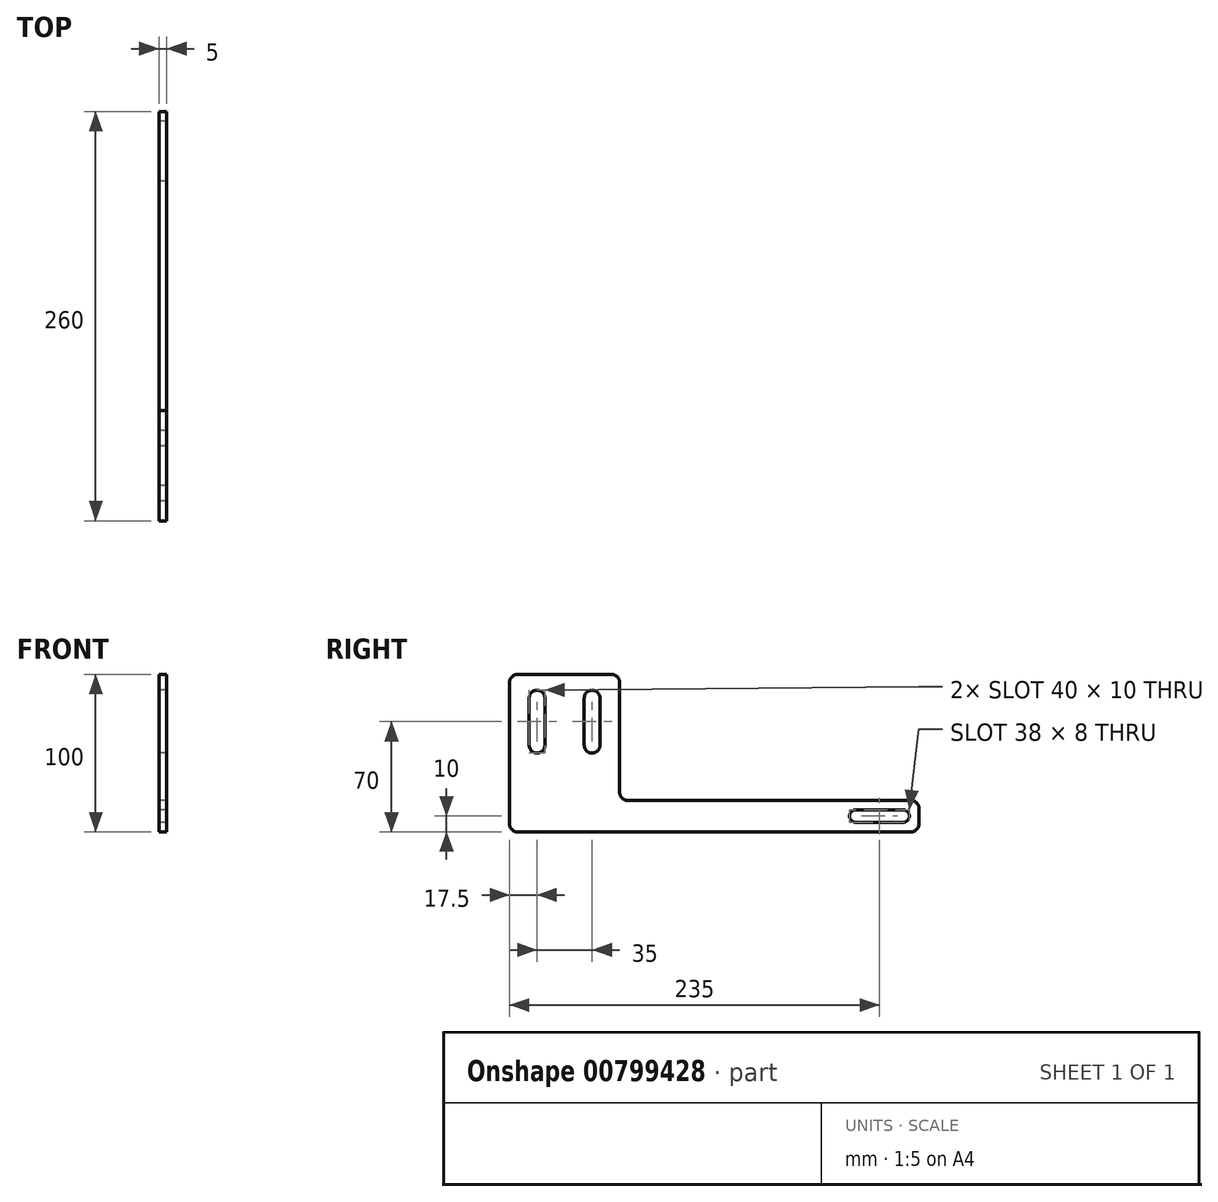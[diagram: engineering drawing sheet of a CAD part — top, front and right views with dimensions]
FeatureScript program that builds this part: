
annotation { "Feature Type Name" : "Feature", "Feature Type Description" : "" }
export const myFeature = defineFeature(function(context is Context, id is Id, definition is map)
    precondition{}
    {
        {
            var Q0;
            Q0=qCreatedBy(makeId("Right.planeOp"),FACE);
            var sketch = newSketch(context, id + "F0", { "sketchPlane" : qUnion([Q0])});
            skLineSegment(sketch, "E0", {"start": v(-130, 95) * mm, "end": v(-130, 5) * mm});
            skLineSegment(sketch, "E1", {"start": v(-125, 0) * mm, "end": v(125, 0) * mm});
            skLineSegment(sketch, "E2", {"start": v(130, 5) * mm, "end": v(130, 15) * mm});
            skLineSegment(sketch, "E3", {"start": v(125, 20) * mm, "end": v(-55, 20) * mm});
            skLineSegment(sketch, "E4", {"start": v(-60, 25) * mm, "end": v(-60, 95) * mm});
            skLineSegment(sketch, "E5", {"start": v(-65, 100) * mm, "end": v(-125, 100) * mm});
            skLineSegment(sketch, "E6", {"start": v(130, 10) * mm, "end": v(-130, 10) * mm, "construction": true});
            skLineSegment(sketch, "E7.bottom", {"start": v(120, 14) * mm, "end": v(90, 14) * mm});
            skLineSegment(sketch, "E7.top", {"start": v(120, 6) * mm, "end": v(90, 6) * mm});
            skPoint(sketch, "E7.middle", {"position": v(105, 10) * mm});
            skArc(sketch, "E8", {"start": v(120, 6) * mm, "mid": v(124, 10) * mm, "end": v(120, 14) * mm});
            skArc(sketch, "E9", {"start": v(90, 14) * mm, "mid": v(86, 10) * mm, "end": v(90, 6) * mm});
            skLineSegment(sketch, "E10", {"start": v(120, 14) * mm, "end": v(120, 6) * mm, "construction": true});
            skLineSegment(sketch, "E11", {"start": v(90, 6) * mm, "end": v(90, 14) * mm, "construction": true});
            skLineSegment(sketch, "E12", {"start": v(-95, 100) * mm, "end": v(-95, 0) * mm, "construction": true});
            skLineSegment(sketch, "E13", {"start": v(-112.5, 70) * mm, "end": v(-77.5, 70) * mm, "construction": true});
            skPoint(sketch, "E14", {"position": v(-95, 70) * mm});
            skCircle(sketch, "E15", {"center": v(-112.5, 70) * mm, "radius": 5 * mm, "construction": true});
            skCircle(sketch, "E16", {"center": v(-77.5, 70) * mm, "radius": 5 * mm, "construction": true});
            skLineSegment(sketch, "E17.bottom", {"start": v(-107.5, 85) * mm, "end": v(-117.5, 85) * mm, "construction": true});
            skLineSegment(sketch, "E17.top", {"start": v(-107.5, 55) * mm, "end": v(-117.5, 55) * mm, "construction": true});
            skLineSegment(sketch, "E17.left", {"start": v(-107.5, 85) * mm, "end": v(-107.5, 55) * mm});
            skLineSegment(sketch, "E17.right", {"start": v(-117.5, 85) * mm, "end": v(-117.5, 55) * mm});
            skLineSegment(sketch, "E18.bottom", {"start": v(-72.5, 85) * mm, "end": v(-82.5, 85) * mm, "construction": true});
            skLineSegment(sketch, "E18.top", {"start": v(-72.5, 55) * mm, "end": v(-82.5, 55) * mm, "construction": true});
            skLineSegment(sketch, "E18.left", {"start": v(-72.5, 85) * mm, "end": v(-72.5, 55) * mm});
            skLineSegment(sketch, "E18.right", {"start": v(-82.5, 85) * mm, "end": v(-82.5, 55) * mm});
            skArc(sketch, "E19", {"start": v(-107.5, 85) * mm, "mid": v(-112.5, 90) * mm, "end": v(-117.5, 85) * mm});
            skArc(sketch, "E20", {"start": v(-72.5, 85) * mm, "mid": v(-77.5, 90) * mm, "end": v(-82.5, 85) * mm});
            skArc(sketch, "E21", {"start": v(-82.5, 55) * mm, "mid": v(-77.5, 50) * mm, "end": v(-72.5, 55) * mm});
            skArc(sketch, "E22", {"start": v(-117.5, 55) * mm, "mid": v(-112.5, 50) * mm, "end": v(-107.5, 55) * mm});
            skPoint(sketch, "E23.visualSharp", {"position": v(130, 20) * mm});
            skArc(sketch, "E23.filletArc", {"start": v(130, 15) * mm, "mid": v(128.54, 18.54) * mm, "end": v(125, 20) * mm});
            skPoint(sketch, "E24.visualSharp", {"position": v(130, 0) * mm});
            skArc(sketch, "E24.filletArc", {"start": v(125, 0) * mm, "mid": v(128.54, 1.46) * mm, "end": v(130, 5) * mm});
            skPoint(sketch, "E25.visualSharp", {"position": v(-130, 0) * mm});
            skArc(sketch, "E25.filletArc", {"start": v(-130, 5) * mm, "mid": v(-128.54, 1.46) * mm, "end": v(-125, 0) * mm});
            skPoint(sketch, "E26.visualSharp", {"position": v(-130, 100) * mm});
            skArc(sketch, "E26.filletArc", {"start": v(-125, 100) * mm, "mid": v(-128.54, 98.54) * mm, "end": v(-130, 95) * mm});
            skPoint(sketch, "E27.visualSharp", {"position": v(-60, 100) * mm});
            skArc(sketch, "E27.filletArc", {"start": v(-60, 95) * mm, "mid": v(-61.46, 98.54) * mm, "end": v(-65, 100) * mm});
            skPoint(sketch, "E28.visualSharp", {"position": v(-60, 20) * mm});
            skArc(sketch, "E28.filletArc", {"start": v(-60, 25) * mm, "mid": v(-58.54, 21.46) * mm, "end": v(-55, 20) * mm});
            skSolve(sketch);
        }
        {
            var Q0;
            Q0=makeQuery(id+"F0.imprint","IMPRINT",FACE,{"disambiguationData":[TD([[makeQuery(id+"F0.imprint","IMPRINT",EDGE,{"derivedFrom":sQuery(id+"F0.wireOp",EDGE,"E0")}),1.0]])]});
            extrude(context, id + "F1", {"entities" : qUnion([Q0]), "depth" : 5 * mm, "offsetDistance" : 25 * mm});
        }
    });
